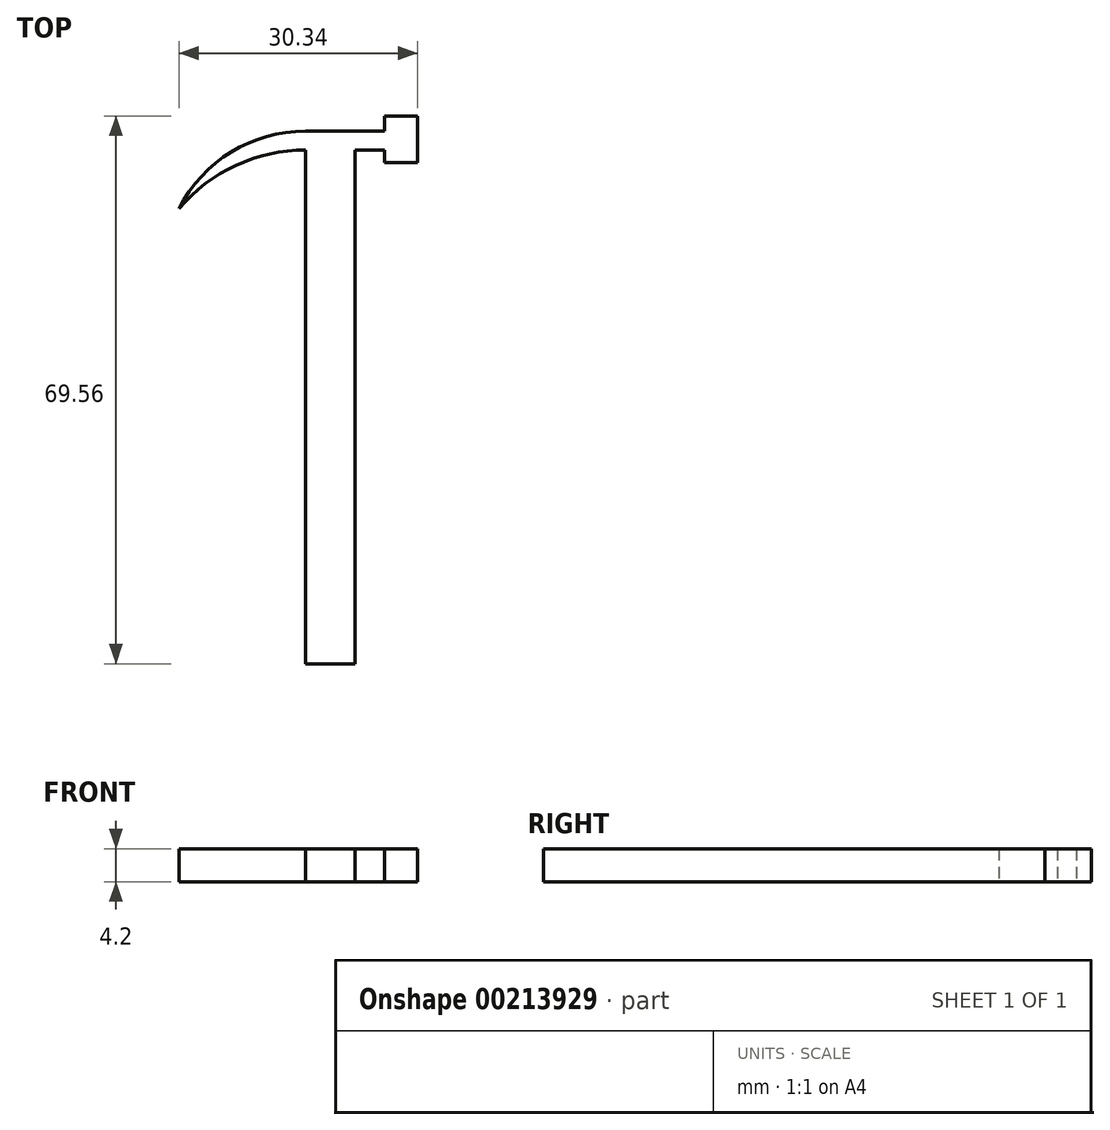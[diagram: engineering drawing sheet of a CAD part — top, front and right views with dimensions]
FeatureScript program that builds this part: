
annotation { "Feature Type Name" : "Feature", "Feature Type Description" : "" }
export const myFeature = defineFeature(function(context is Context, id is Id, definition is map)
    precondition{}
    {
        {
            var Q0;
            Q0=qCreatedBy(makeId("Top.planeOp"),FACE);
            var sketch = newSketch(context, id + "F0", { "sketchPlane" : qUnion([Q0])});
            skLineSegment(sketch, "E0.bottom", {"start": v(-21.75, -38.3) * mm, "end": v(-15.5, -38.3) * mm});
            skLineSegment(sketch, "E0.left", {"start": v(-21.75, -38.3) * mm, "end": v(-21.75, 26.97) * mm});
            skLineSegment(sketch, "E0.right", {"start": v(-15.5, -38.3) * mm, "end": v(-15.5, 26.97) * mm});
            skArc(sketch, "E1", {"start": v(-21.75, 26.97) * mm, "mid": v(-30.62, 25.02) * mm, "end": v(-37.84, 19.52) * mm});
            skLineSegment(sketch, "E2.bottom", {"start": v(-15.5, 26.97) * mm, "end": v(-11.72, 26.97) * mm});
            skLineSegment(sketch, "E2.top", {"start": v(-21.75, 29.37) * mm, "end": v(-11.72, 29.37) * mm});
            skLineSegment(sketch, "E3", {"start": v(-11.72, 26.97) * mm, "end": v(-11.72, 25.37) * mm});
            skLineSegment(sketch, "E4", {"start": v(-11.72, 25.37) * mm, "end": v(-7.5, 25.37) * mm});
            skLineSegment(sketch, "E5", {"start": v(-7.5, 25.37) * mm, "end": v(-7.5, 31.27) * mm});
            skLineSegment(sketch, "E6", {"start": v(-7.5, 31.27) * mm, "end": v(-11.72, 31.27) * mm});
            skLineSegment(sketch, "E7", {"start": v(-11.72, 31.27) * mm, "end": v(-11.72, 29.37) * mm});
            skArc(sketch, "E8", {"start": v(-21.75, 29.37) * mm, "mid": v(-31.19, 26.71) * mm, "end": v(-37.84, 19.52) * mm});
            skSolve(sketch);
        }
        {
            var Q0;
            Q0=makeQuery(id+"F0.imprint","IMPRINT",FACE,{"disambiguationData":[TD([[makeQuery(id+"F0.imprint","IMPRINT",EDGE,{"derivedFrom":sQuery(id+"F0.wireOp",EDGE,"E0.bottom")}),1.0]])]});
            extrude(context, id + "F1", {"entities" : qUnion([Q0]), "depth" : 4.2 * mm});
        }
    });
